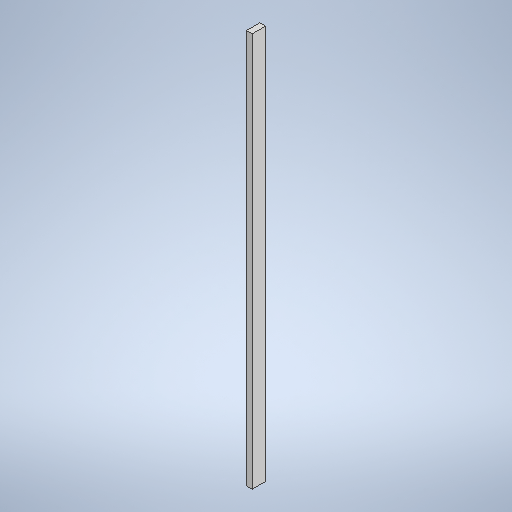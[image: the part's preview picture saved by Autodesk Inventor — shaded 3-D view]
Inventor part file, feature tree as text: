
AUTODESK INVENTOR PART (.ipt)
format: ipt  version: 2025 (Build 290162000, 162)  size: 252,928 bytes
history: native  units: in
note: dims shown in document units (in); Inventor stores cm internally (conversion verified against a paired STEP export)
features: extrude x1, sketch x1
ambient origin geometry x8: Origin, YZ Plane, XZ Plane, XY Plane, X Axis, Y Axis, Z Axis, Center Point
bodies: Solid1 (feature_tree)
feature tree (2):
  extrude  "Extrusion1"  Depth=3.5in
  sketch  "Sketch1"  dims[d0=102.0in d1=3.5in d2=1.5in d3=0.0in]
